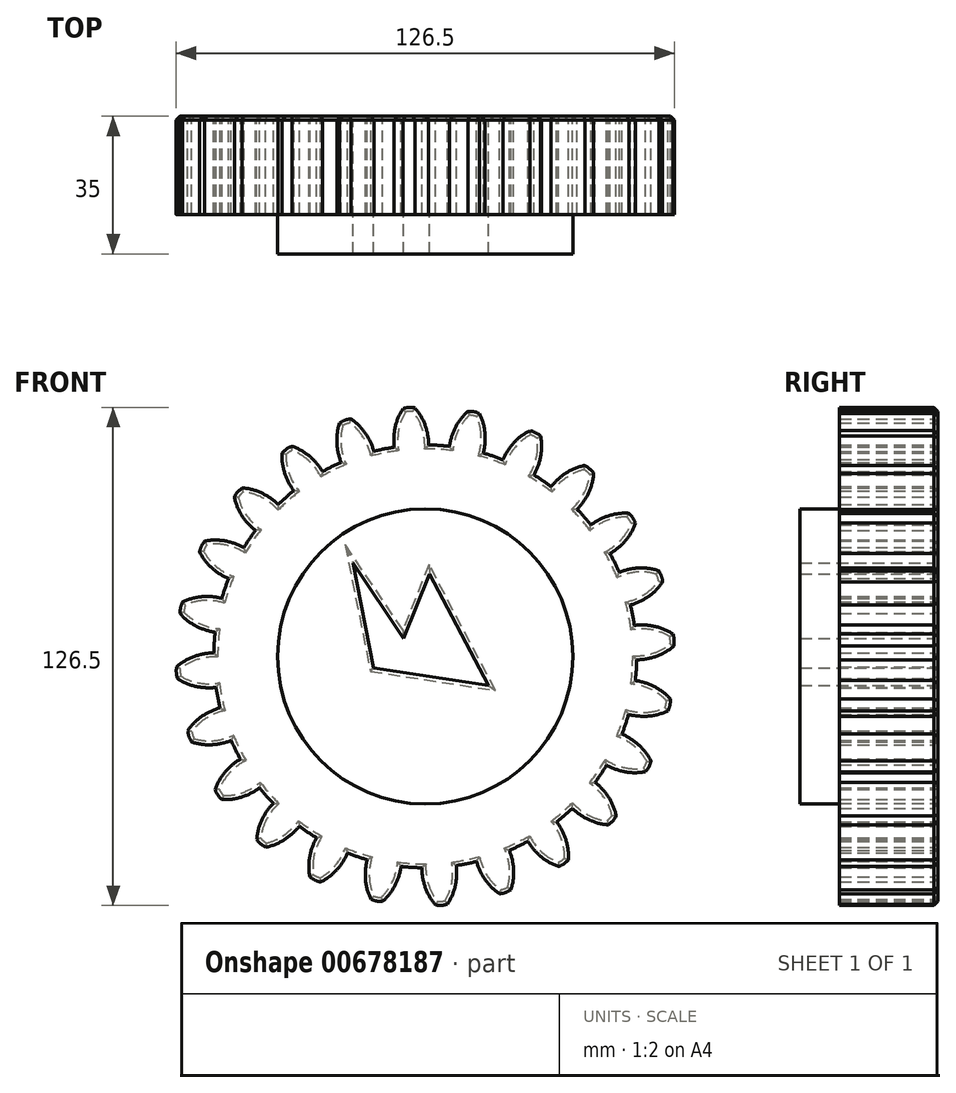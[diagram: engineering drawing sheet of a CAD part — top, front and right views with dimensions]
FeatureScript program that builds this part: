
annotation { "Feature Type Name" : "Feature", "Feature Type Description" : "" }
export const myFeature = defineFeature(function(context is Context, id is Id, definition is map)
    precondition{}
    {
        {
            var Q0;
            Q0=qCreatedBy(makeId("Front.planeOp"),FACE);
            var sketch = newSketch(context, id + "F0", { "sketchPlane" : qUnion([Q0])});
            skCircle(sketch, "E0", {"center": v(0, 0) * mm, "radius": 53.72 * mm});
            skCircle(sketch, "E1", {"center": v(0, 0) * mm, "radius": 58.65 * mm, "construction": true});
            skCircle(sketch, "E2", {"center": v(0, 0) * mm, "radius": 63.5 * mm, "construction": true});
            skLineSegment(sketch, "E3", {"start": v(0, 0) * mm, "end": v(0, 78.84) * mm, "construction": true});
            skLineSegment(sketch, "E4", {"start": v(0, 0) * mm, "end": v(-5.91, 90.2) * mm, "construction": true});
            skPoint(sketch, "E5.startSnap0", {"position": v(0, 39.42) * mm});
            skLineSegment(sketch, "E6", {"start": v(0, 58.65) * mm, "end": v(-64.13, 58.65) * mm, "construction": true});
            skLineSegment(sketch, "E7", {"start": v(0, 58.65) * mm, "end": v(-66.32, 34.51) * mm, "construction": true});
            skCircle(sketch, "E8", {"center": v(0, 0) * mm, "radius": 55.11 * mm, "construction": true});
            skCircle(sketch, "E9", {"center": v(0, 58.65) * mm, "radius": 14.6 * mm, "construction": true});
            skCircle(sketch, "E10", {"center": v(-13.72, 53.65) * mm, "radius": 14.6 * mm, "construction": true});
            skArc(sketch, "E11", {"start": v(0.88, 53.71) * mm, "mid": v(0.64, 56.22) * mm, "end": v(0, 58.65) * mm});
            skArc(sketch, "E12", {"start": v(0, 58.65) * mm, "mid": v(-1.1, 61.03) * mm, "end": v(-2.63, 63.15) * mm});
            skArc(sketch, "E13.MirrorCS", {"start": v(-7.66, 58.15) * mm, "mid": v(-6.88, 60.65) * mm, "end": v(-5.64, 62.95) * mm});
            skCircle(sketch, "E14.MirrorC", {"center": v(6.6, 54.99) * mm, "radius": 14.6 * mm, "construction": true});
            skArc(sketch, "E15.MirrorCS", {"start": v(-7.88, 53.14) * mm, "mid": v(-7.97, 55.65) * mm, "end": v(-7.66, 58.15) * mm});
            skArc(sketch, "E16", {"start": v(-2.63, 63.15) * mm, "mid": v(-4.14, 63.24) * mm, "end": v(-5.64, 62.95) * mm});
            skCircle(sketch, "E17", {"center": v(0, 0) * mm, "radius": 37.5 * mm});
            skLineSegment(sketch, "E18", {"start": v(-18.41, 23.71) * mm, "end": v(-5.46, 4.6) * mm});
            skLineSegment(sketch, "E19", {"start": v(-5.46, 4.6) * mm, "end": v(1.07, 20.93) * mm});
            skLineSegment(sketch, "E20", {"start": v(1.07, 20.93) * mm, "end": v(16.07, -7.38) * mm});
            skLineSegment(sketch, "E21", {"start": v(16.07, -7.38) * mm, "end": v(-13.09, -2.9) * mm});
            skLineSegment(sketch, "E22", {"start": v(-13.09, -2.9) * mm, "end": v(-18.41, 23.71) * mm});
            skSolve(sketch);
        }
        {
            var Q0;
            {var subQ0=sQuery(id+"F0.wireOp",EDGE,"E0");var subQ1=makeQuery(id+"F0.imprint","INTERSECT",VERTEX,{"derivedFrom":[subQ0,sQuery(id+"F0.wireOp",EDGE,"E11")]});Q0=makeQuery(id+"F0.imprint","IMPRINT",FACE,{"disambiguationData":[TD([[makeQuery(id+"F0.imprint","IMPRINT",EDGE,{"disambiguationData":[TD([[subQ1,-1.0]])],"derivedFrom":subQ0}),1.0]])]});}
            var Q1;
            {var subQ0=sQuery(id+"F0.wireOp",EDGE,"E11");Q1=makeQuery(id+"F0.imprint","IMPRINT",FACE,{"disambiguationData":[TD([[makeQuery(id+"F0.imprint","IMPRINT",EDGE,{"derivedFrom":subQ0}),1.0]])]});}
            extrude(context, id + "F1", {"entities" : qUnion([Q0, Q1]), "depth" : 25 * mm, "offsetDistance" : 25 * mm});
        }
        {
            var Q0;
            Q0=makeQuery(id+"F1.opExtrude","SWEPT_BODY",BODY,{"disambiguationData":[OSD([sQuery(id+"F0.wireOp",EDGE,"E0"),sQuery(id+"F0.wireOp",EDGE,"E11"),sQuery(id+"F0.wireOp",EDGE,"E12"),sQuery(id+"F0.wireOp",EDGE,"E13.MirrorCS"),sQuery(id+"F0.wireOp",EDGE,"E15.MirrorCS"),sQuery(id+"F0.wireOp",EDGE,"E16")])]});
            var Q1;
            Q1=makeQuery(id+"F1.opExtrude","SWEPT_FACE",FACE,{"disambiguationData":[OSD([sQuery(id+"F0.wireOp",EDGE,"E0")])]});
            circularPattern(context, id + "F2", {"entities" : qUnion([Q0]), "axis" : qUnion([Q1]), "angle" : 360 * degree, "instanceCount" : 24, "equalSpace" : true});
        }
        {
            var Q0;
            Q0=makeQuery(id+"F0.imprint","IMPRINT",FACE,{"disambiguationData":[TD([[makeQuery(id+"F0.imprint","IMPRINT",EDGE,{"derivedFrom":sQuery(id+"F0.wireOp",EDGE,"E17")}),1.0]])]});
            extrude(context, id + "F3", {"entities" : qUnion([Q0]), "operationType" : NewBodyOperationType.ADD, "depth" : 35 * mm, "offsetDistance" : 25 * mm});
        }
        {
            var Q0;
            {var subQ0=sQuery(id+"F0.wireOp",EDGE,"E17");var subQ1=makeQuery(id+"F1.opExtrude","CAP_FACE",FACE,{"disambiguationData":[OSD([sQuery(id+"F0.wireOp",EDGE,"E0"),sQuery(id+"F0.wireOp",EDGE,"E11"),sQuery(id+"F0.wireOp",EDGE,"E12"),sQuery(id+"F0.wireOp",EDGE,"E13.MirrorCS"),sQuery(id+"F0.wireOp",EDGE,"E15.MirrorCS"),sQuery(id+"F0.wireOp",EDGE,"E16"),subQ0])],"isStart":true});Q0=makeQuery(id+"F3.boolean.opBoolean","MERGE",FACE,{"derivedFrom":[subQ1,makeQuery(id+"F2.opPattern","COPY",FACE,{"derivedFrom":subQ1,"instanceName":"1"}),makeQuery(id+"F2.opPattern","COPY",FACE,{"derivedFrom":subQ1,"instanceName":"2"}),makeQuery(id+"F2.opPattern","COPY",FACE,{"derivedFrom":subQ1,"instanceName":"3"}),makeQuery(id+"F2.opPattern","COPY",FACE,{"derivedFrom":subQ1,"instanceName":"4"}),makeQuery(id+"F2.opPattern","COPY",FACE,{"derivedFrom":subQ1,"instanceName":"5"}),makeQuery(id+"F2.opPattern","COPY",FACE,{"derivedFrom":subQ1,"instanceName":"6"}),makeQuery(id+"F2.opPattern","COPY",FACE,{"derivedFrom":subQ1,"instanceName":"7"}),makeQuery(id+"F2.opPattern","COPY",FACE,{"derivedFrom":subQ1,"instanceName":"8"}),makeQuery(id+"F2.opPattern","COPY",FACE,{"derivedFrom":subQ1,"instanceName":"9"}),makeQuery(id+"F2.opPattern","COPY",FACE,{"derivedFrom":subQ1,"instanceName":"10"}),makeQuery(id+"F2.opPattern","COPY",FACE,{"derivedFrom":subQ1,"instanceName":"11"}),makeQuery(id+"F2.opPattern","COPY",FACE,{"derivedFrom":subQ1,"instanceName":"12"}),makeQuery(id+"F2.opPattern","COPY",FACE,{"derivedFrom":subQ1,"instanceName":"13"}),makeQuery(id+"F2.opPattern","COPY",FACE,{"derivedFrom":subQ1,"instanceName":"14"}),makeQuery(id+"F2.opPattern","COPY",FACE,{"derivedFrom":subQ1,"instanceName":"15"}),makeQuery(id+"F2.opPattern","COPY",FACE,{"derivedFrom":subQ1,"instanceName":"16"}),makeQuery(id+"F2.opPattern","COPY",FACE,{"derivedFrom":subQ1,"instanceName":"17"}),makeQuery(id+"F2.opPattern","COPY",FACE,{"derivedFrom":subQ1,"instanceName":"18"}),makeQuery(id+"F2.opPattern","COPY",FACE,{"derivedFrom":subQ1,"instanceName":"19"}),makeQuery(id+"F2.opPattern","COPY",FACE,{"derivedFrom":subQ1,"instanceName":"20"}),makeQuery(id+"F2.opPattern","COPY",FACE,{"derivedFrom":subQ1,"instanceName":"21"}),makeQuery(id+"F2.opPattern","COPY",FACE,{"derivedFrom":subQ1,"instanceName":"22"}),makeQuery(id+"F2.opPattern","COPY",FACE,{"derivedFrom":subQ1,"instanceName":"23"}),makeQuery(id+"F3.opExtrude","CAP_FACE",FACE,{"disambiguationData":[OSD([subQ0,sQuery(id+"F0.wireOp",EDGE,"E18"),sQuery(id+"F0.wireOp",EDGE,"E19"),sQuery(id+"F0.wireOp",EDGE,"E20"),sQuery(id+"F0.wireOp",EDGE,"E21"),sQuery(id+"F0.wireOp",EDGE,"E22")])],"isStart":true})]});}
            chamfer(context, id + "F4", {"entities" : qUnion([Q0]), "width" : 1 * mm, "tangentPropagation" : true});
        }
    });
